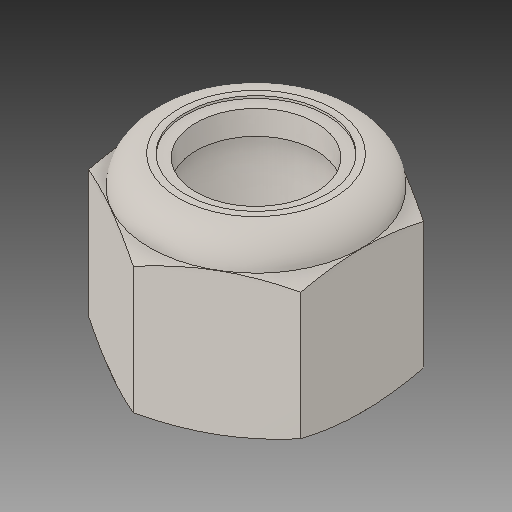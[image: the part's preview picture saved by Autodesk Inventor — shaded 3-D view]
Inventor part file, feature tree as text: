
AUTODESK INVENTOR PART (.ipt)
format: ipt  version: 2018 (Build 220112000, 112)  size: 190,464 bytes
history: native  units: in
note: dims shown in document units (in); Inventor stores cm internally (conversion verified against a paired STEP export)
features: other x1, revolve x1
ambient origin geometry x8: Origin, YZ Plane, XZ Plane, XY Plane, X Axis, Y Axis, Z Axis, Center Point
bodies: Solid1 (feature_tree), Solid2 (feature_tree)
feature tree (2):
  other  "Cut-Revolve2"
  revolve  "Revolve1"  [1 undecoded]
note: 1 required parameter value undecoded (feature->parameter linkage not recoverable at this tier; creation-order binding heuristic only, values carry confidence <= 0.55)
